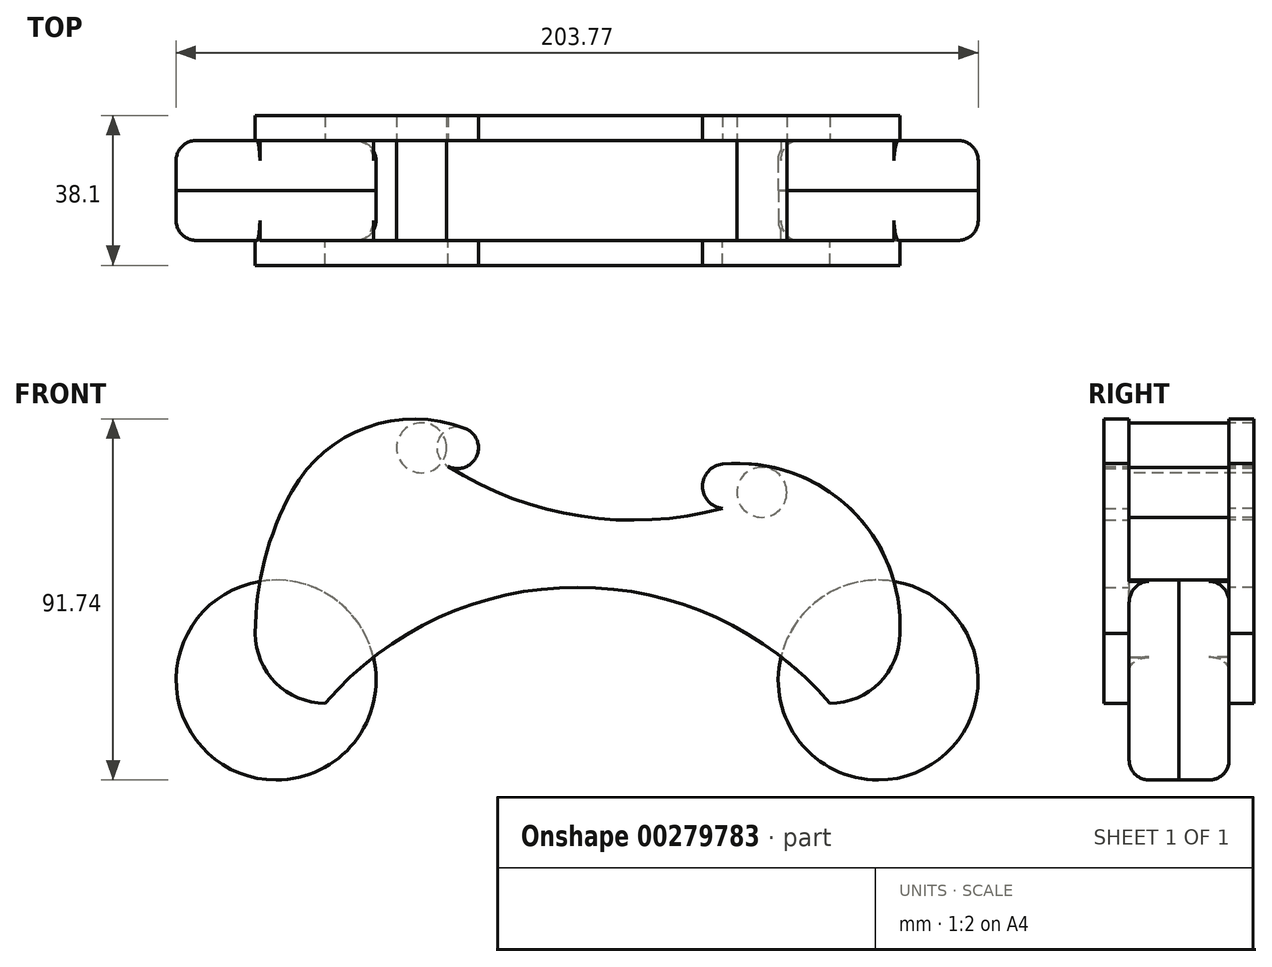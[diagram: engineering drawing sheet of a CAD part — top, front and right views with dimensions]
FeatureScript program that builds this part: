
annotation { "Feature Type Name" : "Feature", "Feature Type Description" : "" }
export const myFeature = defineFeature(function(context is Context, id is Id, definition is map)
    precondition{}
    {
        {
            var Q0;
            Q0=qCreatedBy(makeId("Front.planeOp"),FACE);
            var sketch = newSketch(context, id + "F0", { "sketchPlane" : qUnion([Q0])});
            skCircle(sketch, "E0", {"center": v(-62.06, 12.71) * mm, "radius": 25.4 * mm});
            skCircle(sketch, "E1", {"center": v(90.91, 12.71) * mm, "radius": 25.4 * mm});
            skSolve(sketch);
        }
        {
            var Q0;
            Q0=qCreatedBy(makeId("Front.planeOp"),FACE);
            var sketch = newSketch(context, id + "F1", { "sketchPlane" : qUnion([Q0])});
            skLineSegment(sketch, "E2", {"start": v(-61.83, 12.6) * mm, "end": v(90.57, 12.6) * mm, "construction": true});
            skLineSegment(sketch, "E3", {"start": v(-61.83, 12.6) * mm, "end": v(-61.83, 88.8) * mm, "construction": true});
            skLineSegment(sketch, "E4", {"start": v(-61.83, 88.8) * mm, "end": v(90.57, 88.8) * mm, "construction": true});
            skLineSegment(sketch, "E5", {"start": v(90.57, 88.8) * mm, "end": v(90.57, 12.6) * mm, "construction": true});
            skLineSegment(sketch, "E6.top", {"start": v(-67.35, 67.55) * mm, "end": v(-53.08, 67.55) * mm});
            skLineSegment(sketch, "E6.right", {"start": v(96.45, 24.59) * mm, "end": v(96.45, 28.48) * mm});
            skArc(sketch, "E7.filletArc", {"start": v(-67.35, 24.59) * mm, "mid": v(-62.14, 12.02) * mm, "end": v(-49.57, 6.8) * mm});
            skArc(sketch, "E8.filletArc", {"start": v(78.67, 6.8) * mm, "mid": v(91.24, 12.02) * mm, "end": v(96.45, 24.59) * mm});
            skArc(sketch, "E9", {"start": v(78.67, 6.8) * mm, "mid": v(14.55, 36.27) * mm, "end": v(-49.57, 6.8) * mm});
            skArc(sketch, "E10", {"start": v(-67.35, 24.59) * mm, "mid": v(-64.97, 43.26) * mm, "end": v(-58, 60.75) * mm});
            skArc(sketch, "E11", {"start": v(-58, 60.75) * mm, "mid": v(-38.99, 76.94) * mm, "end": v(-14.02, 76.64) * mm});
            skArc(sketch, "E12", {"start": v(51.38, 67.55) * mm, "mid": v(83.72, 56.36) * mm, "end": v(96.45, 24.59) * mm});
            skArc(sketch, "E13", {"start": v(51.38, 67.55) * mm, "mid": v(46.27, 61.93) * mm, "end": v(51.38, 56.31) * mm});
            skArc(sketch, "E14", {"start": v(-14.02, 76.64) * mm, "mid": v(-11.35, 69.1) * mm, "end": v(-19.2, 67.55) * mm});
            skArc(sketch, "E15", {"start": v(-19.2, 67.55) * mm, "mid": v(14.9, 54.42) * mm, "end": v(51.38, 56.31) * mm});
            skPoint(sketch, "E16", {"position": v(-37.44, 18.38) * mm});
            skPoint(sketch, "E17", {"position": v(-66.13, 38.02) * mm});
            skPoint(sketch, "E18", {"position": v(66.54, 18.38) * mm});
            skPoint(sketch, "E19", {"position": v(94.83, 38.12) * mm});
            skArc(sketch, "E20", {"start": v(-19.2, 67.55) * mm, "mid": v(-32.04, 44.35) * mm, "end": v(-37.44, 18.38) * mm});
            skArc(sketch, "E21", {"start": v(-37.44, 18.38) * mm, "mid": v(-45.89, 36.82) * mm, "end": v(-66.13, 38.02) * mm});
            skArc(sketch, "E22", {"start": v(-19.2, 67.55) * mm, "mid": v(-36.14, 71.8) * mm, "end": v(-53.08, 67.55) * mm});
            skSolve(sketch);
        }
        {
            var Q0;
            Q0 = qSketchRegion(id + "F1", true);
            extrude(context, id + "F2", {"entities" : qUnion([Q0]), "depth" : 6.35 * mm});
        }
        {
            var Q0;
            Q0 = qSketchRegion(id + "F0", true);
            extrude(context, id + "F3", {"entities" : qUnion([Q0]), "oppositeDirection" : true, "depth" : 12.7 * mm});
        }
        {
            var Q0;
            Q0=makeQuery(id+"F2.opExtrude","SWEPT_BODY",BODY,{"disambiguationData":[OSD([sQuery(id+"F1.wireOp",EDGE,"E7.filletArc"),sQuery(id+"F1.wireOp",EDGE,"E8.filletArc"),sQuery(id+"F1.wireOp",EDGE,"E9"),sQuery(id+"F1.wireOp",EDGE,"E10"),sQuery(id+"F1.wireOp",EDGE,"E11"),sQuery(id+"F1.wireOp",EDGE,"E12"),sQuery(id+"F1.wireOp",EDGE,"E13"),sQuery(id+"F1.wireOp",EDGE,"E14"),sQuery(id+"F1.wireOp",EDGE,"E15")])]});
            var Q1;
            Q1=makeQuery(id+"F3.opExtrude","CAP_FACE",FACE,{"disambiguationData":[OSD([sQuery(id+"F0.wireOp",EDGE,"E0")])],"isStart":false});
            mirror(context, id + "F4", {"operationType" : NewBodyOperationType.ADD, "entities" : qUnion([Q0]), "mirrorPlane" : qUnion([Q1])});
        }
        {
            var Q0;
            {var subQ0=sQuery(id+"F0.wireOp",EDGE,"E1");Q0=makeQuery(id+"F3.boolean.opBoolean","SPLIT",EDGE,{"disambiguationData":[topologyDisambiguationEdgeConnected([makeQuery(id+"F3.opExtrude","CAP_FACE",FACE,{"disambiguationData":[OSD([subQ0])],"isStart":true})])],"derivedFrom":makeQuery(id+"F3.opExtrude","CAP_EDGE",EDGE,{"disambiguationData":[OSD([subQ0])],"isStart":true})});}
            var Q1;
            {var subQ0=sQuery(id+"F0.wireOp",EDGE,"E0");Q1=makeQuery(id+"F3.boolean.opBoolean","SPLIT",EDGE,{"disambiguationData":[topologyDisambiguationEdgeConnected([makeQuery(id+"F3.opExtrude","CAP_FACE",FACE,{"disambiguationData":[OSD([subQ0])],"isStart":true})])],"derivedFrom":makeQuery(id+"F3.opExtrude","CAP_EDGE",EDGE,{"disambiguationData":[OSD([subQ0])],"isStart":true})});}
            var Q2;
            {var subQ0=sQuery(id+"F0.wireOp",EDGE,"E0");Q2=makeQuery(id+"F4.opPattern","COPY",EDGE,{"derivedFrom":makeQuery(id+"F3.boolean.opBoolean","SPLIT",EDGE,{"disambiguationData":[topologyDisambiguationEdgeConnected([makeQuery(id+"F3.opExtrude","CAP_FACE",FACE,{"disambiguationData":[OSD([subQ0])],"isStart":true})])],"derivedFrom":makeQuery(id+"F3.opExtrude","CAP_EDGE",EDGE,{"disambiguationData":[OSD([subQ0])],"isStart":true})}),"instanceName":"1"});}
            var Q3;
            {var subQ0=sQuery(id+"F0.wireOp",EDGE,"E1");Q3=makeQuery(id+"F4.opPattern","COPY",EDGE,{"derivedFrom":makeQuery(id+"F3.boolean.opBoolean","SPLIT",EDGE,{"disambiguationData":[topologyDisambiguationEdgeConnected([makeQuery(id+"F3.opExtrude","CAP_FACE",FACE,{"disambiguationData":[OSD([subQ0])],"isStart":true})])],"derivedFrom":makeQuery(id+"F3.opExtrude","CAP_EDGE",EDGE,{"disambiguationData":[OSD([subQ0])],"isStart":true})}),"instanceName":"1"});}
            fillet(context, id + "F5", {"entities" : qUnion([Q0, Q1, Q2, Q3]), "radius" : 5.08 * mm, "tangentPropagation" : true, "allowEdgeOverflow" : false});
        }
        {
            var Q0;
            Q0=qCreatedBy(makeId("Front.planeOp"),FACE);
            var sketch = newSketch(context, id + "F6", { "sketchPlane" : qUnion([Q0])});
            skCircle(sketch, "E23", {"center": v(-25.1, 71.72) * mm, "radius": 6.35 * mm});
            skCircle(sketch, "E24", {"center": v(61.34, 60.4) * mm, "radius": 6.35 * mm});
            skSolve(sketch);
        }
        {
            var Q0;
            Q0 = qSketchRegion(id + "F6", true);
            extrude(context, id + "F7", {"entities" : qUnion([Q0]), "oppositeDirection" : true, "depth" : 31.75 * mm});
        }
        {
            var Q0;
            Q0=makeQuery(id+"F3.opExtrude","SWEPT_BODY",BODY,{"disambiguationData":[OSD([sQuery(id+"F0.wireOp",EDGE,"E0")])]});
            var Q1;
            Q1=makeQuery(id+"F3.opExtrude","SWEPT_BODY",BODY,{"disambiguationData":[OSD([sQuery(id+"F0.wireOp",EDGE,"E1")])]});
            var Q2;
            Q2=makeQuery(id+"F3.opExtrude","CAP_FACE",FACE,{"disambiguationData":[OSD([sQuery(id+"F0.wireOp",EDGE,"E0")])],"isStart":false});
            mirror(context, id + "F8", {"entities" : qUnion([Q0, Q1]), "mirrorPlane" : qUnion([Q2])});
        }
    });
